FCSTD DOCUMENT  (FreeCAD 0.16RUnknown)
Label: holder
License: All rights reserved
LicenseURL: http://en.wikipedia.org/wiki/All_rights_reserved
objects: Sketcher::SketchObject×2, Spreadsheet::Sheet×1
note: 2 computed .brp shape members not serialized (recipe doc carries the construction recipe); baked Part::Feature solids carry a one-line shape summary decoded from their .brp

FEATURE [Sketcher::SketchObject] Sketch  label="plate"
  expr: Constraints[9] = size.length
  expr: Constraints[8] = size.width
  sketch-geometry (4):
    g0: LineSegment StartX=-300.048 StartY=106.66 StartZ=0 EndX=119.952 EndY=106.66 EndZ=0
    g1: LineSegment StartX=119.952 StartY=106.66 StartZ=0 EndX=119.952 EndY=-313.34 EndZ=0
    g2: LineSegment StartX=119.952 StartY=-313.34 StartZ=0 EndX=-300.048 EndY=-313.34 EndZ=0
    g3: LineSegment StartX=-300.048 StartY=-313.34 StartZ=0 EndX=-300.048 EndY=106.66 EndZ=0
  constraints (10):
    c: Coincident(g0,g1)
    c: Coincident(g1,g2)
    c: Coincident(g2,g3)
    c: Coincident(g3,g0)
    c: Horizontal(g0)
    c: Horizontal(g2)
    c: Vertical(g1)
    c: Vertical(g3)
    c: DistanceY(g1,g0) = 420
    c: DistanceX(g0,g0) = 420
FEATURE [Spreadsheet::Sheet] Spreadsheet  label="prefs"
  cells = A1=width; B1(width)=420; A2=depth; B2(depth)=420; A3=thickness; B3(thickness)=5; A4=boxWidth; B4(boxWidth)=100; A5=boxDepth; B5(boxDepth)=70; A6=wallThickness; B6(wallThickness)=6; A7=boxHeight; B7(boxHeight)=50
FEATURE [Sketcher::SketchObject] Sketch001  label="sideWidth"
  expr: Constraints[53] = prefs.boxHeight - prefs.thickness
  expr: Constraints[51] = prefs.boxHeight + prefs.thickness
  expr: Constraints[41] = prefs.boxWidth + 2 * prefs.wallThickness
  sketch-geometry (20):
    g0: LineSegment StartX=0 StartY=-30.4443 StartZ=0 EndX=37.3333 EndY=-30.4443 EndZ=0
    g1: LineSegment StartX=37.3333 StartY=-30.4443 StartZ=0 EndX=37.3333 EndY=-25.4443 EndZ=0
    g2: LineSegment StartX=37.3333 StartY=-25.4443 StartZ=0 EndX=74.6667 EndY=-25.4443 EndZ=0
    g3: LineSegment StartX=74.6667 StartY=-25.4443 StartZ=0 EndX=74.6667 EndY=-30.4443 EndZ=0
    g4: LineSegment StartX=74.6667 StartY=-30.4443 StartZ=0 EndX=112 EndY=-30.4443 EndZ=0
    g5: LineSegment StartX=112 StartY=24.5557 StartZ=0 EndX=74.6667 EndY=24.5557 EndZ=0
    g6: LineSegment StartX=74.6667 StartY=24.5557 StartZ=0 EndX=74.6667 EndY=19.5557 EndZ=0
    g7: LineSegment StartX=74.6667 StartY=19.5557 StartZ=0 EndX=37.3333 EndY=19.5557 EndZ=0
    g8: LineSegment StartX=37.3333 StartY=19.5557 StartZ=0 EndX=37.3333 EndY=24.5557 EndZ=0
    g9: LineSegment StartX=37.3333 StartY=24.5557 StartZ=0 EndX=0 EndY=24.5557 EndZ=0
    g10: LineSegment StartX=0 StartY=24.5557 StartZ=0 EndX=0 EndY=0 EndZ=0
    g11: LineSegment StartX=0 StartY=0 StartZ=0 EndX=6 EndY=0 EndZ=0
    g12: LineSegment StartX=6 StartY=0 StartZ=0 EndX=6 EndY=-5.88857 EndZ=0
    g13: LineSegment StartX=6 StartY=-5.88857 StartZ=0 EndX=0 EndY=-5.88857 EndZ=0
    g14: LineSegment StartX=0 StartY=-5.88857 StartZ=0 EndX=0 EndY=-30.4443 EndZ=0
    g15: LineSegment StartX=112 StartY=24.5557 StartZ=0 EndX=112 EndY=0 EndZ=0
    g16: LineSegment StartX=112 StartY=0 StartZ=0 EndX=106 EndY=0 EndZ=0
    g17: LineSegment StartX=106 StartY=0 StartZ=0 EndX=106 EndY=-5.88857 EndZ=0
    g18: LineSegment StartX=106 StartY=-5.88857 StartZ=0 EndX=112 EndY=-5.88857 EndZ=0
    g19: LineSegment StartX=112 StartY=-5.88857 StartZ=0 EndX=112 EndY=-30.4443 EndZ=0
  constraints (58):
    c: Coincident(g0,g1)
    c: Vertical(g1)
    c: Coincident(g1,g2)
    c: Coincident(g2,g3)
    c: Vertical(g3)
    c: Coincident(g3,g4)
    c: Horizontal(g4)
    c: Horizontal(g5)
    c: Coincident(g5,g6)
    c: Vertical(g6)
    c: Coincident(g6,g7)
    c: Coincident(g7,g8)
    c: Vertical(g8)
    c: Coincident(g8,g9)
    c: Coincident(g9,g10)
    c: Vertical(g10)
    c: Coincident(g10,g11)
    c: PointOnObject(g11,g-1)
    c: Coincident(g11,g12)
    c: Coincident(g12,g13)
    c: Coincident(g13,g14)
    c: Coincident(g14,g0)
    c: Vertical(g14)
    c: Coincident(g5,g15)
    c: Vertical(g15)
    c: Coincident(g15,g16)
    c: Horizontal(g16)
    c: Coincident(g16,g17)
    c: Vertical(g17)
    c: Coincident(g17,g18)
    c: Coincident(g18,g19)
    c: Coincident(g19,g4)
    c: Horizontal(g9)
    c: Horizontal(g11)
    c: Horizontal(g13)
    c: Horizontal(g18)
    c: Horizontal(g7)
    c: Horizontal(g2)
    c: Vertical(g12)
    c: Horizontal(g0)
    c: Vertical(g19)
    c: DistanceX(g9,g5) = 112
    c: Equal(g9,g0)
    c: Equal(g5,g4)
    c: DistanceX(g11,g16) = 100
    c: Equal(g11,g16)
    c: Equal(g11,g13)
    c: Equal(g15,g19)
    c: Equal(g10,g14)
    c: Equal(g12,g17)
    c: Equal(g14,g19)
    c: DistanceY(g0,g8) = 55
    c: Equal(g8,g1)
    c: DistanceY(g1,g7) = 45
    c: Equal(g6,g3)
    c: DistanceX(g0,g-1) = 0
    c: Equal(g2,g7)
    c: Equal(g0,g4)
